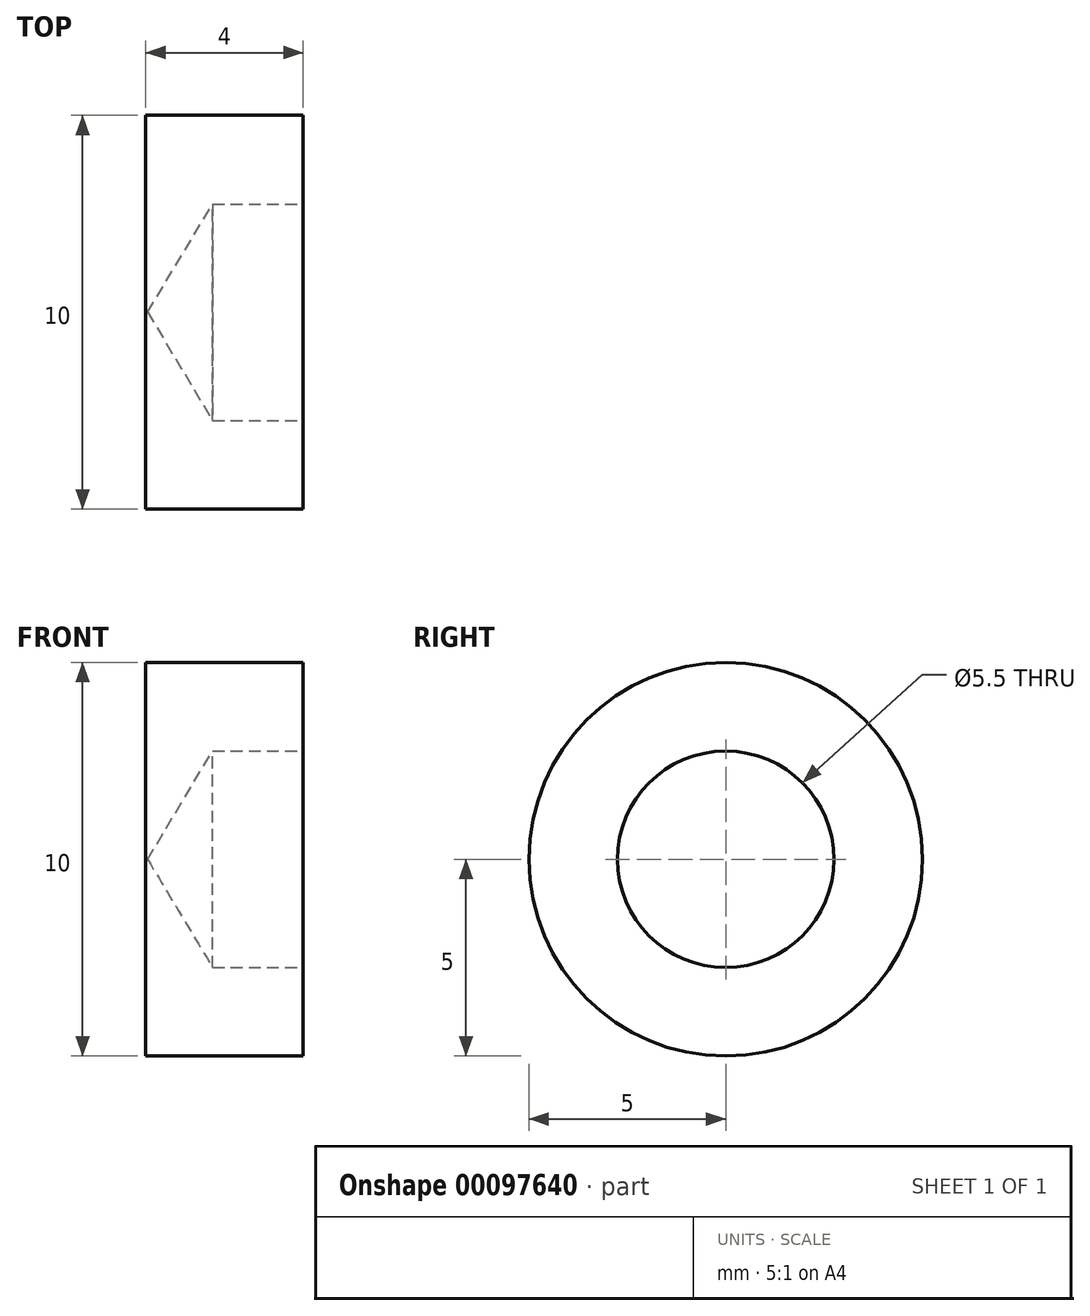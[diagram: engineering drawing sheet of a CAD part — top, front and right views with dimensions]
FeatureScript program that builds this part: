
annotation { "Feature Type Name" : "Feature", "Feature Type Description" : "" }
export const myFeature = defineFeature(function(context is Context, id is Id, definition is map)
    precondition{}
    {
        {
            var Q0;
            Q0=qCreatedBy(makeId("Right.planeOp"),FACE);
            var sketch = newSketch(context, id + "F0", { "sketchPlane" : qUnion([Q0])});
            skCircle(sketch, "E0", {"center": v(0, 0) * mm, "radius": 5 * mm});
            skSolve(sketch);
        }
        {
            var Q0;
            Q0=makeQuery(id+"F0.imprint","IMPRINT",FACE,{"disambiguationData":[TD([[makeQuery(id+"F0.imprint","IMPRINT",EDGE,{"derivedFrom":sQuery(id+"F0.wireOp",EDGE,"E0")}),1.0]])]});
            extrude(context, id + "F1", {"entities" : qUnion([Q0]), "oppositeDirection" : true, "depth" : 4 * mm});
        }
        {
            var Q0;
            Q0=sQuery(id+"F0.wireOp",VERTEX,"E0.center");
            var Q1;
            Q1=makeQuery(id+"F1.opExtrude","SWEPT_BODY",BODY,{"disambiguationData":[OSD([sQuery(id+"F0.wireOp",EDGE,"E0")])]});
            hole(context, id + "F2", {"style" : HoleStyle.SIMPLE, "endStyle" : HoleEndStyle.BLIND, "standardTappedOrClearance" : lookupTablePath({ "standard" : "ISO", "fit" : "Normal", "size" : "M5", "type" : "Clearance" }), "standardBlindInLast" : lookupTablePath({ "fit" : "Standard", "standard" : "ISO", "size" : "M5", "type" : "Clearance" }), "holeDiameter" : 5.5 * mm, "holeDepth" : 2.3 * mm, "locations" : qUnion([Q0]), "scope" : qUnion([Q1])});
        }
    });
